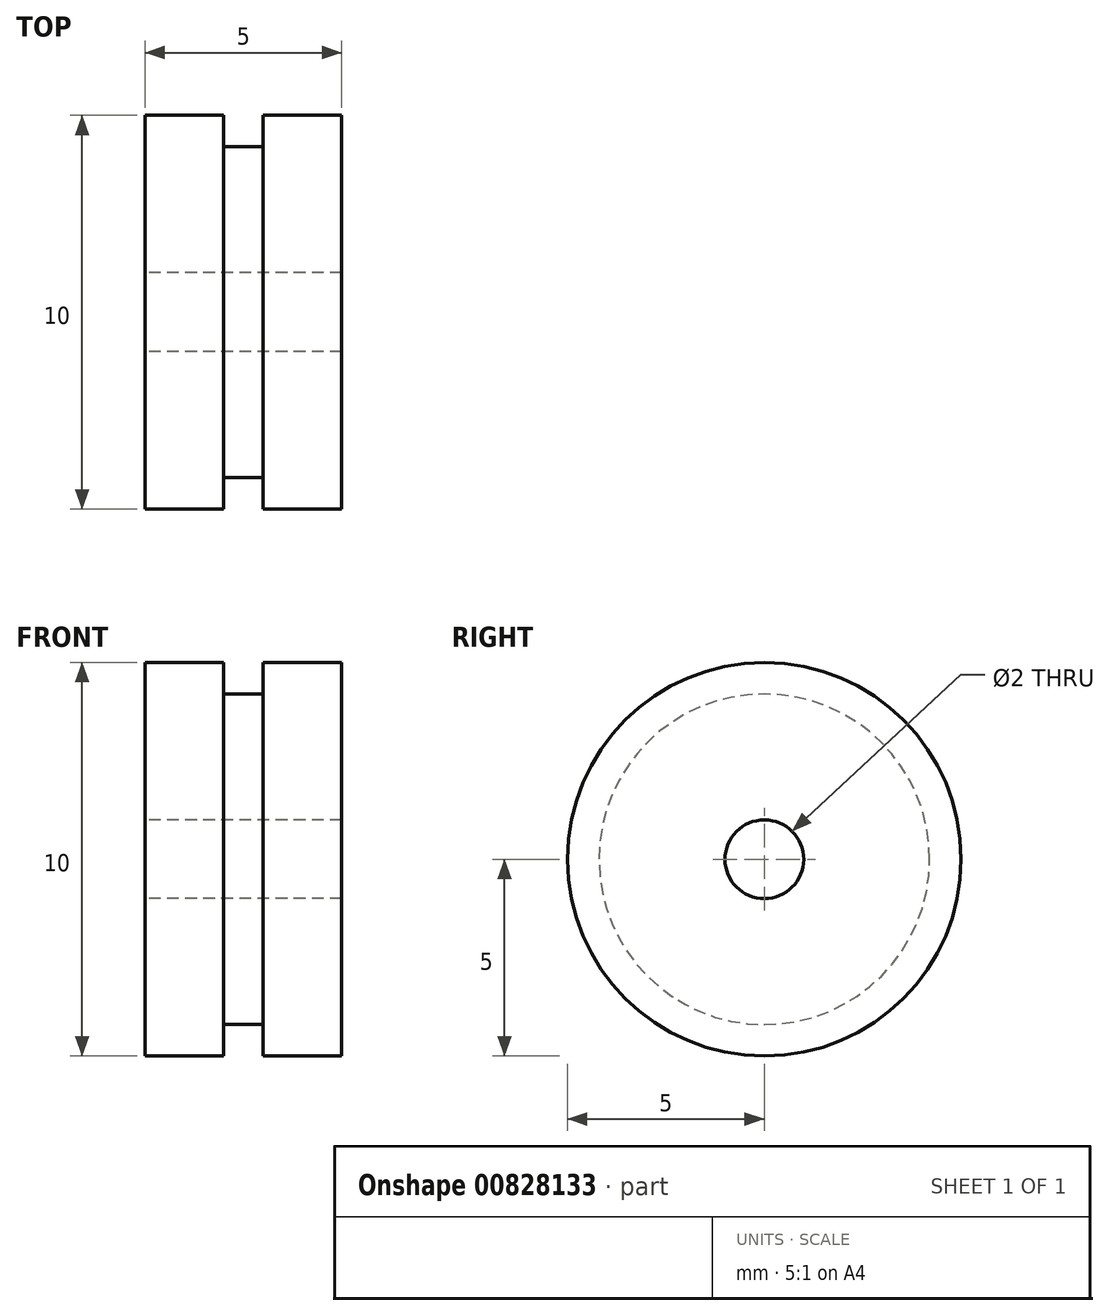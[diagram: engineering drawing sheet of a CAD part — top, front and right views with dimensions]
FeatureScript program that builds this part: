
annotation { "Feature Type Name" : "Feature", "Feature Type Description" : "" }
export const myFeature = defineFeature(function(context is Context, id is Id, definition is map)
    precondition{}
    {
        {
            var Q0;
            Q0=qCreatedBy(makeId("Front.planeOp"),FACE);
            var sketch = newSketch(context, id + "F0", { "sketchPlane" : qUnion([Q0])});
            skLineSegment(sketch, "E0", {"start": v(-3.7, 0) * mm, "end": v(3.74, 0) * mm, "construction": true});
            skLineSegment(sketch, "E1", {"start": v(-2.5, 0) * mm, "end": v(-2.5, 5) * mm});
            skLineSegment(sketch, "E2", {"start": v(-2.5, 5) * mm, "end": v(-0.5, 5) * mm});
            skLineSegment(sketch, "E3", {"start": v(-0.5, 5) * mm, "end": v(-0.5, 4.2) * mm});
            skLineSegment(sketch, "E4", {"start": v(-0.5, 4.2) * mm, "end": v(0.5, 4.2) * mm});
            skLineSegment(sketch, "E5", {"start": v(0.5, 4.2) * mm, "end": v(0.5, 5) * mm});
            skLineSegment(sketch, "E6", {"start": v(0.5, 5) * mm, "end": v(2.5, 5) * mm});
            skLineSegment(sketch, "E7", {"start": v(2.5, 5) * mm, "end": v(2.5, 0) * mm});
            skLineSegment(sketch, "E8", {"start": v(2.5, 0) * mm, "end": v(-2.5, 0) * mm});
            skSolve(sketch);
        }
        {
            var Q0;
            Q0 = qSketchRegion(id + "F0", true);
            var Q1;
            Q1=sQuery(id+"F0.wireOp",EDGE,"E0");
            revolve(context, id + "F1", {"surfaceOperationType" : NewSurfaceOperationType.NEW, "entities" : qUnion([Q0]), "axis" : qUnion([Q1]), "revolveType" : RevolveType.FULL});
        }
        {
            var Q0;
            Q0=makeQuery(id+"F1.opRevolve","SWEPT_FACE",FACE,{"disambiguationData":[OSD([sQuery(id+"F0.wireOp",EDGE,"E1")])]});
            var sketch = newSketch(context, id + "F2", { "sketchPlane" : qUnion([Q0])});
            skPoint(sketch, "E9", {"position": v(0, 0) * mm});
            skSolve(sketch);
        }
        {
            var Q0;
            Q0=sQuery(id+"F2.wireOp",VERTEX,"E9");
            var Q1;
            Q1=makeQuery(id+"F1.opRevolve","SWEPT_BODY",BODY,{"disambiguationData":[OSD([sQuery(id+"F0.wireOp",EDGE,"E1"),sQuery(id+"F0.wireOp",EDGE,"E2"),sQuery(id+"F0.wireOp",EDGE,"E3"),sQuery(id+"F0.wireOp",EDGE,"E4"),sQuery(id+"F0.wireOp",EDGE,"E5"),sQuery(id+"F0.wireOp",EDGE,"E6"),sQuery(id+"F0.wireOp",EDGE,"E7"),sQuery(id+"F0.wireOp",EDGE,"E8")])]});
            hole(context, id + "F3", {"style" : HoleStyle.SIMPLE, "endStyle" : HoleEndStyle.THROUGH, "standardTappedOrClearance" : lookupTablePath({ "standard" : "ISO", "size" : "2", "type" : "Drilled" }), "standardBlindInLast" : lookupTablePath({ "standard" : "ISO", "size" : "2", "type" : "Drilled" }), "holeDiameter" : 2 * mm, "majorDiameter" : 5 * mm, "isTappedThrough" : true, "tappedDepth" : 7.3 * mm, "tapClearance" : 3, "locations" : qUnion([Q0]), "scope" : qUnion([Q1])});
        }
    });
